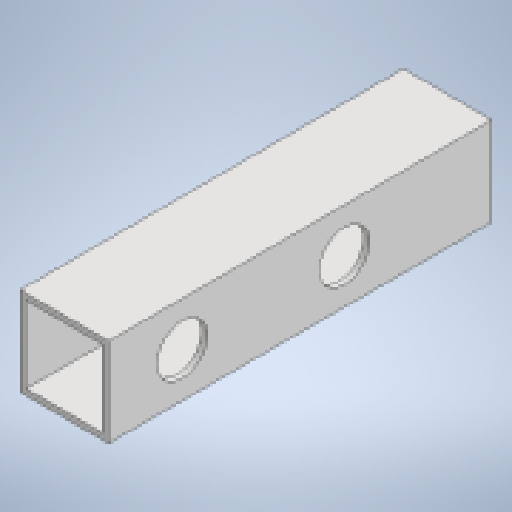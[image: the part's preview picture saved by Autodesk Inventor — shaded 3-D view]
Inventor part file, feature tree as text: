
AUTODESK INVENTOR PART (.ipt)
format: ipt  version: 2025.4 (Build 294407000, 407)  size: 181,760 bytes
history: native  units: mm
features: extrude x2, sketch x2, pattern_linear x1
ambient origin geometry x8: Origin, YZ Plane, XZ Plane, XY Plane, X Axis, Y Axis, Z Axis, Center Point
bodies: Body1 (feature_tree)
feature tree (5):
  extrude  "Extrusion3"  Depth=30.0mm
  extrude  "Extrusion4"  Depth=2.0mm
  pattern_linear  "Rectangular Pattern4"  Count1=13 Spacing1=0.0mm
  sketch  "Sketch9"  dims[d61=500.0mm d172=30.0mm]
  sketch  "Sketch10"  dims[d173=30.0mm d174=2.0mm d175=130.0mm d176=0.0mm d177=17.0mm d178=17.0mm d179=0.0mm d180=0.0mm d181=30.0mm d182=80.0mm d186=17.0mm d187=20.0mm d189=55.0mm]
